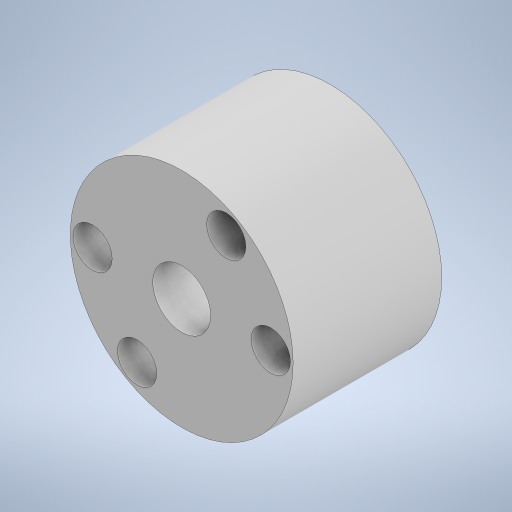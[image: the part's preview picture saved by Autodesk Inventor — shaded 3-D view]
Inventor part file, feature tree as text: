
AUTODESK INVENTOR PART (.ipt)
format: ipt  version: 2023 (Build 270158000, 158)  size: 245,248 bytes
history: native  units: in
note: dims shown in document units (in); Inventor stores cm internally (conversion verified against a paired STEP export)
features: extrude x1, sketch x1
ambient origin geometry x8: Origin, YZ Plane, XZ Plane, XY Plane, X Axis, Y Axis, Z Axis, Center Point
bodies: Body1 (feature_tree)
feature tree (2):
  extrude  "Extrusion14"  Depth=0.3in
  sketch  "Sketch1"  dims[d3=0.866in d15=0.75in d37=0.75in d69=0.132in d70=0.132in d73=0.5in d74=0.0in d75=0.132in d76=0.132in d79=0.3in d80=0.3in d82=0.195in d83=0.3in d84=0.3in]
